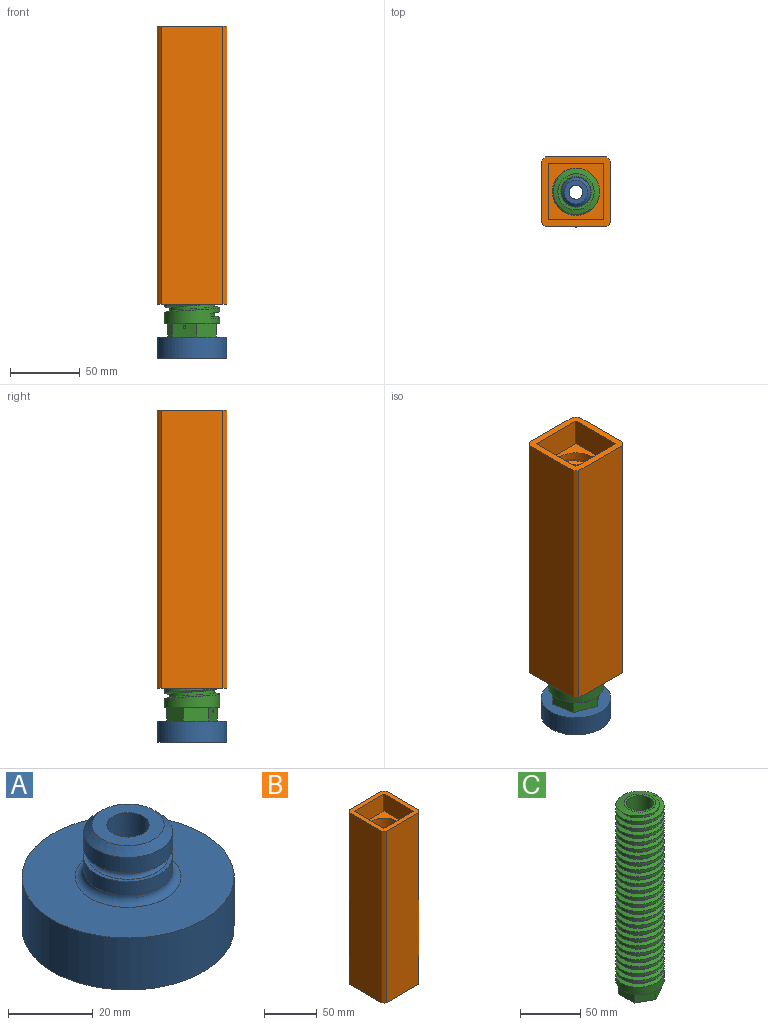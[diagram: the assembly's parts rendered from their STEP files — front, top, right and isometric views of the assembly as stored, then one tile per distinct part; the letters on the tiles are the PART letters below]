
ASSEMBLY  parts=3 mates=3
PART A: 15 faces, bbox 50x50x30 mm
  f0: cylinder r=10.5mm len=21mm, axis (0,0,-1), area 296.9mm2, adj f6,f10
  f1: cylinder r=25mm len=50mm, axis (0,0,-1), area 2356.2mm2, adj f2,f3
  f2: plane 50x50mm, normal (0,0,1), area 1472.6mm2, adj f1,f7
  f3: plane 50x50mm, normal (0,0,-1), area 706.9mm2, adj f1,f9
  f4: cylinder r=10.5mm len=21mm, axis (0,0,-1), area 263.9mm2, adj f7,f11
  f5: plane 17x17mm, normal (0,0,1), area 148.4mm2, adj f6,f8
  f6: cone r=8.5mm half-angle=45deg, axis (0,0,-1), area 168.8mm2, adj f0,f5
  f7: torus R=12.5mm, axis (0,0,1), area 221.6mm2, adj f2,f4
  f8: cylinder r=5mm len=15mm, axis (0,0,-1), area 471.2mm2, adj f5,f9
  f9: cone r=5mm half-angle=45deg, axis (0,0,-1), area 1666.1mm2, adj f3,f8
  f10: plane 21x21mm, normal (0,0,-1), area 62.8mm2, adj f0,f14
  f11: plane 21x21mm, normal (0,0,1), area 62.8mm2, adj f4,f12
  f12: torus R=9.5mm, axis (0,0,1), area 87.5mm2, adj f11,f13
  f13: cylinder r=8.5mm len=17mm, axis (0,0,1), area 26.7mm2, adj f12,f14
  f14: torus R=9.5mm, axis (0,0,1), area 87.5mm2, adj f10,f13
PART B: 46 faces, bbox 50x50x200.9 mm
  f0: plane 200x43.95mm, normal (0,1,0), area 8789.5mm2, adj f4,f5,f43,f44
  f1: plane 200x43.95mm, normal (-1,0,0), area 8789.5mm2, adj f4,f5,f44,f45
  f2: plane 200x43.95mm, normal (0,-1,0), area 8789.5mm2, adj f4,f5,f42,f45
  f3: plane 200x43.95mm, normal (1,0,0), area 8789.5mm2, adj f4,f5,f42,f43
  f4: plane 50x50mm, normal (0,0,1), area 882.5mm2, adj f0,f1,f2,f3,f37,f38,f39,f40
  f5: plane 50x50mm, normal (0,0,-1), area 1117mm2, adj f0,f1,f2,f3,f36,f42,f43,f44
  f6: cylinder r=17mm len=34mm, axis (0,0,-1), area 272.6mm2, adj f7,f31,f32,f34,f36
  f7: cylinder r=17mm len=34mm, axis (0,0,-1), area 281.3mm2, adj f6,f8,f32,f34
  f8: cylinder r=17mm len=34mm, axis (0,0,-1), area 280.9mm2, adj f7,f9,f32,f34
  f9: cylinder r=17mm len=34mm, axis (0,0,-1), area 280.6mm2, adj f8,f10,f32,f34
  f10: cylinder r=17mm len=34mm, axis (0,0,-1), area 280.9mm2, adj f9,f11,f32,f34
  f11: cylinder r=17mm len=34mm, axis (0,0,-1), area 280.6mm2, adj f10,f12,f32,f34
  f12: cylinder r=17mm len=34mm, axis (0,0,-1), area 281.3mm2, adj f11,f13,f32,f34
  f13: cylinder r=17mm len=34mm, axis (0,0,-1), area 281mm2, adj f12,f14,f32,f34
  f14: cylinder r=17mm len=34mm, axis (0,0,-1), area 281mm2, adj f13,f15,f32,f34
  f15: cylinder r=17mm len=34mm, axis (0,0,-1), area 280.9mm2, adj f14,f16,f32,f34
  f16: cylinder r=17mm len=34mm, axis (0,0,-1), area 280.5mm2, adj f15,f17,f32,f34
  f17: cylinder r=17mm len=34mm, axis (0,0,-1), area 281mm2, adj f16,f18,f32,f34
  f18: cylinder r=17mm len=34mm, axis (0,0,-1), area 280.9mm2, adj f17,f19,f32,f34
  f19: cylinder r=17mm len=34mm, axis (0,0,-1), area 281.2mm2, adj f18,f20,f32,f34
  f20: cylinder r=17mm len=34mm, axis (0,0,-1), area 281.1mm2, adj f19,f21,f32,f34
  f21: cylinder r=17mm len=34mm, axis (0,0,-1), area 280.7mm2, adj f20,f22,f32,f34
  f22: cylinder r=17mm len=34mm, axis (0,0,-1), area 280.9mm2, adj f21,f23,f32,f34
  f23: cylinder r=17mm len=34mm, axis (0,0,-1), area 280.5mm2, adj f22,f24,f32,f34
  f24: cylinder r=17mm len=34mm, axis (0,0,-1), area 281.2mm2, adj f23,f25,f32,f34
  f25: cylinder r=17mm len=34mm, axis (0,0,-1), area 281.1mm2, adj f24,f26,f32,f34
  f26: cylinder r=17mm len=34mm, axis (0,0,-1), area 281mm2, adj f25,f27,f32,f34
  f27: cylinder r=17mm len=34mm, axis (0,0,-1), area 281.1mm2, adj f26,f28,f32,f34
  f28: cylinder r=17mm len=34mm, axis (0,0,-1), area 280.5mm2, adj f27,f29,f32,f34
  f29: cylinder r=17mm len=34mm, axis (0,0,-1), area 280.9mm2, adj f28,f30,f32,f34
  f30: cylinder r=17mm len=34mm, axis (0,0,-1), area 907.8mm2, adj f29,f32,f35,f41
  f31: cylinder r=17mm len=16.86mm, axis (0,0,-1), area 19.6mm2, adj f6,f34,f36
  f32: bspline ~175.87x46.77mm, area 9797.2mm2, adj f6,f7,f8,f9,f10,f11,f12,f13
  f33: cylinder r=20.25mm len=173.97mm, axis (0,0,1), area 8310mm2, adj f32,f34,f35,f36
  f34: bspline ~172.37x46.77mm, area 9606mm2, adj f6,f7,f8,f9,f10,f11,f12,f13
  f35: plane 4.37x3.25mm, normal (0,-1,0), area 11.4mm2, adj f30,f32,f33,f34
  f36: cone r=15.25mm half-angle=75deg, axis (0,0,-1), area 277.7mm2, adj f5,f6,f31,f32,f33,f34
  f37: plane 40x20mm, normal (1,0,0), area 800mm2, adj f4,f38,f40,f41
  f38: plane 40x20mm, normal (0,1,0), area 800mm2, adj f4,f37,f39,f41
  f39: plane 40x20mm, normal (-1,0,0), area 800mm2, adj f4,f38,f40,f41
  f40: plane 40x20mm, normal (0,-1,0), area 800mm2, adj f4,f37,f39,f41
  f41: plane 40x40mm, normal (0,0,1), area 692.1mm2, adj f30,f37,f38,f39,f40
  f42: cylinder r=33.28mm len=200mm, axis (0,0,1), area 856.6mm2, adj f2,f3,f4,f5
  f43: cylinder r=33.28mm len=200mm, axis (0,0,1), area 856.6mm2, adj f0,f3,f4,f5
  f44: cylinder r=33.28mm len=200mm, axis (0,0,1), area 856.6mm2, adj f0,f1,f4,f5
  f45: cylinder r=33.28mm len=200mm, axis (0,0,1), area 856.6mm2, adj f1,f2,f4,f5
PART C: 44 faces, bbox 40x46.2x191.3 mm
  f0: cylinder r=20mm len=40mm, axis (0,0,-1), area 832.4mm2, adj f1,f27,f29,f32
  f1: cylinder r=20mm len=40mm, axis (0,0,-1), area 334.3mm2, adj f0,f2,f30,f32
  f2: cylinder r=20mm len=40mm, axis (0,0,-1), area 334.1mm2, adj f1,f3,f30,f32
  f3: cylinder r=20mm len=40mm, axis (0,0,-1), area 334.2mm2, adj f2,f4,f30,f32
  f4: cylinder r=20mm len=40mm, axis (0,0,-1), area 333.9mm2, adj f3,f5,f30,f32
  f5: cylinder r=20mm len=40mm, axis (0,0,-1), area 334.1mm2, adj f4,f6,f30,f32
  f6: cylinder r=20mm len=40mm, axis (0,0,-1), area 333.8mm2, adj f5,f7,f30,f32
  f7: cylinder r=20mm len=40mm, axis (0,0,-1), area 334.2mm2, adj f6,f8,f30,f32
  f8: cylinder r=20mm len=40mm, axis (0,0,-1), area 333.8mm2, adj f7,f9,f30,f32
  f9: cylinder r=20mm len=40mm, axis (0,0,-1), area 334.3mm2, adj f8,f10,f30,f32
  f10: cylinder r=20mm len=40mm, axis (0,0,-1), area 333.9mm2, adj f9,f11,f30,f32
  f11: cylinder r=20mm len=40mm, axis (0,0,-1), area 334.5mm2, adj f10,f12,f30,f32
  f12: cylinder r=20mm len=40mm, axis (0,0,-1), area 334mm2, adj f11,f13,f30,f32
  f13: cylinder r=20mm len=40mm, axis (0,0,-1), area 334.6mm2, adj f12,f14,f30,f32
  f14: cylinder r=20mm len=40mm, axis (0,0,-1), area 334.2mm2, adj f13,f15,f30,f32
  f15: cylinder r=20mm len=40mm, axis (0,0,-1), area 334.7mm2, adj f14,f16,f30,f32
  f16: cylinder r=20mm len=40mm, axis (0,0,-1), area 334.3mm2, adj f15,f17,f30,f32
  f17: cylinder r=20mm len=40mm, axis (0,0,-1), area 334.8mm2, adj f16,f18,f30,f32
  f18: cylinder r=20mm len=40mm, axis (0,0,-1), area 334.4mm2, adj f17,f19,f30,f32
  f19: cylinder r=20mm len=40mm, axis (0,0,-1), area 334.7mm2, adj f18,f20,f30,f32
  f20: cylinder r=20mm len=40mm, axis (0,0,-1), area 334.3mm2, adj f19,f21,f30,f32
  f21: cylinder r=20mm len=40mm, axis (0,0,-1), area 334.6mm2, adj f20,f22,f30,f32
  f22: cylinder r=20mm len=40mm, axis (0,0,-1), area 334.2mm2, adj f21,f23,f30,f32
  f23: cylinder r=20mm len=40mm, axis (0,0,-1), area 334.3mm2, adj f22,f24,f30,f32
  f24: cylinder r=20mm len=40mm, axis (0,0,-1), area 334.1mm2, adj f23,f25,f30,f32
  f25: cylinder r=20mm len=34.7mm, axis (0,0,-1), area 63.7mm2, adj f24,f28,f30
  f26: plane 26x26mm, normal (0,0,1), area 150.8mm2, adj f28,f40
  f27: plane 40x40mm, normal (0,0,-1), area 369.8mm2, adj f0,f33,f34,f35,f36,f37,f38
  f28: cone r=13mm half-angle=75deg, axis (0,0,-1), area 538.8mm2, adj f25,f26,f30,f31,f32
  f29: plane 4.34x3.75mm, normal (0,1,0), area 12.5mm2, adj f0,f30,f31,f32
  f30: bspline ~174.84x46.19mm, area 10867.8mm2, adj f1,f2,f3,f4,f5,f6,f7,f8
  f31: cylinder r=16.25mm len=175mm, axis (0,0,-1), area 8929.3mm2, adj f28,f29,f30,f32
  f32: bspline ~176.01x46.19mm, area 11072.5mm2, adj f0,f1,f2,f3,f4,f5,f6,f7
  f33: plane 16x10mm, normal (-0.5,-0.87,0), area 184.8mm2, adj f27,f34,f38,f39
  f34: plane 16x10mm, normal (0.5,-0.87,0), area 181.6mm2, adj f27,f33,f35,f39,f42
  f35: plane 18.48x10mm, normal (1,0,0), area 184.8mm2, adj f27,f34,f36,f39
  f36: plane 16x10mm, normal (0.5,0.87,0), area 184.8mm2, adj f27,f35,f37,f39
  f37: plane 16x10mm, normal (-0.5,0.87,0), area 181.6mm2, adj f27,f36,f38,f39,f43
  f38: plane 18.48x10mm, normal (-1,0,0), area 184.8mm2, adj f27,f33,f37,f39
  f39: plane 36.95x32mm, normal (0,0,-1), area 395.9mm2, adj f33,f34,f35,f36,f37,f38,f41
  f40: cylinder r=11mm len=188.5mm, axis (0,0,-1), area 13021.9mm2, adj f26,f41,f42,f43
  f41: cone r=11mm half-angle=45deg, axis (0,0,-1), area 156.6mm2, adj f39,f40
  f42: cylinder r=1mm len=5.37mm, axis (0.5,-0.87,0), area 31.7mm2, adj f34,f40
  f43: cylinder r=1mm len=5.37mm, axis (0.5,-0.87,0), area 31.7mm2, adj f37,f40
PLACE A rot(axis=(0,0,-1),139.9deg) t=(0,0,-38.63)mm
PLACE B rot(axis=(0,0,1),90deg) t=(0,0,0)mm
PLACE C rot(axis=(0,0,-1),49.9deg) t=(0,0,-23.63)mm
MATE cylindrical C.f40 <-> B.f6  axis (0,0,1) through (0,0,166.37)mm
MATE parallel C.f0 <-> B.f42  axis (0,0,1) through (0,0,166.37)mm
MATE parallel A.f1 <-> C.f40  axis (0,0,1) through (0,0,-23.63)mm
